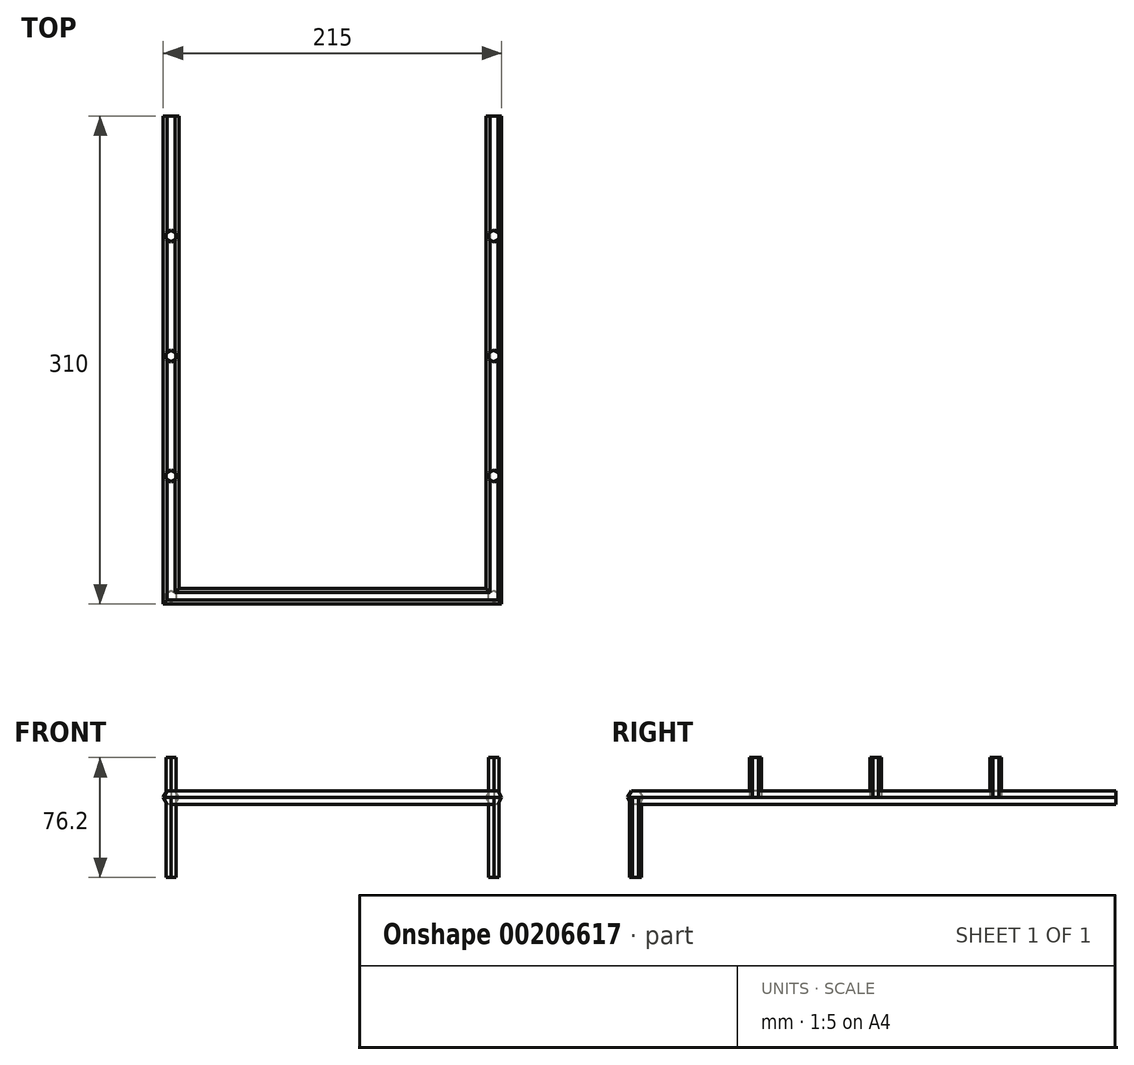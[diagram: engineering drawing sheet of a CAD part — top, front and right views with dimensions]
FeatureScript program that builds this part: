
annotation { "Feature Type Name" : "Feature", "Feature Type Description" : "" }
export const myFeature = defineFeature(function(context is Context, id is Id, definition is map)
    precondition{}
    {
        {
            var Q0;
            Q0=qCreatedBy(makeId("Top.planeOp"),FACE);
            var sketch = newSketch(context, id + "F0", { "sketchPlane" : qUnion([Q0])});
            skLineSegment(sketch, "E0.top", {"start": v(0, -305) * mm, "end": v(-205, -305) * mm});
            skLineSegment(sketch, "E0.left", {"start": v(0, 0) * mm, "end": v(0, -305) * mm});
            skLineSegment(sketch, "E0.right", {"start": v(-205, 0) * mm, "end": v(-205, -305) * mm});
            skPoint(sketch, "E1", {"position": v(0, -305) * mm});
            skPoint(sketch, "E2", {"position": v(0, 0) * mm});
            skPoint(sketch, "E3", {"position": v(0, -152.5) * mm});
            skPoint(sketch, "E4", {"position": v(-102.5, -305) * mm});
            skPoint(sketch, "E5", {"position": v(-205, -305) * mm});
            skPoint(sketch, "E6", {"position": v(-205, 0) * mm});
            skPoint(sketch, "E7", {"position": v(-205, -152.5) * mm});
            skPoint(sketch, "E8", {"position": v(0, -76.25) * mm});
            skPoint(sketch, "E9", {"position": v(-205, -76.25) * mm});
            skPoint(sketch, "E10", {"position": v(-205, -228.75) * mm});
            skPoint(sketch, "E11", {"position": v(0, -228.75) * mm});
            skPoint(sketch, "E12", {"position": v(-51.1, -305) * mm});
            skPoint(sketch, "E13", {"position": v(-153.6, -305) * mm});
            skCircle(sketch, "E14.cCircle", {"center": v(0, -76.25) * mm, "radius": 3.75 * mm, "construction": true});
            skLineSegment(sketch, "E14.0", {"start": v(0, -72.5) * mm, "end": v(3.25, -74.37) * mm});
            skLineSegment(sketch, "E14.1", {"start": v(3.25, -74.38) * mm, "end": v(3.25, -78.12) * mm});
            skLineSegment(sketch, "E14.2", {"start": v(3.25, -78.12) * mm, "end": v(0, -80) * mm});
            skLineSegment(sketch, "E14.3", {"start": v(0, -80) * mm, "end": v(-3.25, -78.13) * mm});
            skLineSegment(sketch, "E14.4", {"start": v(-3.25, -78.12) * mm, "end": v(-3.25, -74.38) * mm});
            skLineSegment(sketch, "E14.5", {"start": v(-3.25, -74.38) * mm, "end": v(0, -72.5) * mm});
            skCircle(sketch, "E15.cCircle", {"center": v(0, -228.75) * mm, "radius": 3.75 * mm, "construction": true});
            skLineSegment(sketch, "E15.0", {"start": v(0, -232.5) * mm, "end": v(-3.25, -230.62) * mm});
            skLineSegment(sketch, "E15.1", {"start": v(-3.25, -230.63) * mm, "end": v(-3.25, -226.88) * mm});
            skLineSegment(sketch, "E15.2", {"start": v(-3.25, -226.88) * mm, "end": v(0, -225) * mm});
            skLineSegment(sketch, "E15.3", {"start": v(0, -225) * mm, "end": v(3.25, -226.88) * mm});
            skLineSegment(sketch, "E15.4", {"start": v(3.25, -226.88) * mm, "end": v(3.25, -230.62) * mm});
            skLineSegment(sketch, "E15.5", {"start": v(3.25, -230.62) * mm, "end": v(0, -232.5) * mm});
            skCircle(sketch, "E16.cCircle", {"center": v(0, -152.5) * mm, "radius": 3.75 * mm, "construction": true});
            skLineSegment(sketch, "E16.0", {"start": v(0, -156.25) * mm, "end": v(-3.25, -154.38) * mm});
            skLineSegment(sketch, "E16.1", {"start": v(-3.25, -154.37) * mm, "end": v(-3.25, -150.62) * mm});
            skLineSegment(sketch, "E16.2", {"start": v(-3.25, -150.62) * mm, "end": v(0, -148.75) * mm});
            skLineSegment(sketch, "E16.3", {"start": v(0, -148.75) * mm, "end": v(3.25, -150.62) * mm});
            skLineSegment(sketch, "E16.4", {"start": v(3.25, -150.62) * mm, "end": v(3.25, -154.37) * mm});
            skLineSegment(sketch, "E16.5", {"start": v(3.25, -154.37) * mm, "end": v(0, -156.25) * mm});
            skCircle(sketch, "E17.cCircle", {"center": v(-205, -228.75) * mm, "radius": 3.75 * mm, "construction": true});
            skLineSegment(sketch, "E17.0", {"start": v(-205, -225) * mm, "end": v(-201.75, -226.88) * mm});
            skLineSegment(sketch, "E17.1", {"start": v(-201.75, -226.88) * mm, "end": v(-201.75, -230.63) * mm});
            skLineSegment(sketch, "E17.2", {"start": v(-201.75, -230.63) * mm, "end": v(-205, -232.5) * mm});
            skLineSegment(sketch, "E17.3", {"start": v(-205, -232.5) * mm, "end": v(-208.25, -230.63) * mm});
            skLineSegment(sketch, "E17.4", {"start": v(-208.25, -230.63) * mm, "end": v(-208.25, -226.88) * mm});
            skLineSegment(sketch, "E17.5", {"start": v(-208.25, -226.88) * mm, "end": v(-205, -225) * mm});
            skCircle(sketch, "E18.cCircle", {"center": v(-205, -152.5) * mm, "radius": 3.75 * mm, "construction": true});
            skLineSegment(sketch, "E18.0", {"start": v(-205, -148.75) * mm, "end": v(-201.75, -150.62) * mm});
            skLineSegment(sketch, "E18.1", {"start": v(-201.75, -150.63) * mm, "end": v(-201.75, -154.38) * mm});
            skLineSegment(sketch, "E18.2", {"start": v(-201.75, -154.38) * mm, "end": v(-205, -156.25) * mm});
            skLineSegment(sketch, "E18.3", {"start": v(-205, -156.25) * mm, "end": v(-208.25, -154.38) * mm});
            skLineSegment(sketch, "E18.4", {"start": v(-208.25, -154.38) * mm, "end": v(-208.25, -150.63) * mm});
            skLineSegment(sketch, "E18.5", {"start": v(-208.25, -150.63) * mm, "end": v(-205, -148.75) * mm});
            skCircle(sketch, "E19.cCircle", {"center": v(-205, -76.25) * mm, "radius": 3.75 * mm, "construction": true});
            skLineSegment(sketch, "E19.0", {"start": v(-205, -80) * mm, "end": v(-208.25, -78.12) * mm});
            skLineSegment(sketch, "E19.1", {"start": v(-208.25, -78.12) * mm, "end": v(-208.25, -74.38) * mm});
            skLineSegment(sketch, "E19.2", {"start": v(-208.25, -74.38) * mm, "end": v(-205, -72.5) * mm});
            skLineSegment(sketch, "E19.3", {"start": v(-205, -72.5) * mm, "end": v(-201.75, -74.38) * mm});
            skLineSegment(sketch, "E19.4", {"start": v(-201.75, -74.38) * mm, "end": v(-201.75, -78.12) * mm});
            skLineSegment(sketch, "E19.5", {"start": v(-201.75, -78.12) * mm, "end": v(-205, -80) * mm});
            skCircle(sketch, "E20.cCircle", {"center": v(-205, -305) * mm, "radius": 3.75 * mm, "construction": true});
            skLineSegment(sketch, "E20.0", {"start": v(-205, -301.25) * mm, "end": v(-201.75, -303.12) * mm});
            skLineSegment(sketch, "E20.1", {"start": v(-201.75, -303.12) * mm, "end": v(-201.75, -306.87) * mm});
            skLineSegment(sketch, "E20.2", {"start": v(-201.75, -306.87) * mm, "end": v(-205, -308.75) * mm});
            skLineSegment(sketch, "E20.3", {"start": v(-205, -308.75) * mm, "end": v(-208.25, -306.88) * mm});
            skLineSegment(sketch, "E20.4", {"start": v(-208.25, -306.88) * mm, "end": v(-208.25, -303.12) * mm});
            skLineSegment(sketch, "E20.5", {"start": v(-208.25, -303.12) * mm, "end": v(-205, -301.25) * mm});
            skCircle(sketch, "E21.cCircle", {"center": v(0, -305) * mm, "radius": 3.75 * mm, "construction": true});
            skLineSegment(sketch, "E21.0", {"start": v(0, -301.25) * mm, "end": v(3.25, -303.13) * mm});
            skLineSegment(sketch, "E21.1", {"start": v(3.25, -303.13) * mm, "end": v(3.25, -306.88) * mm});
            skLineSegment(sketch, "E21.2", {"start": v(3.25, -306.87) * mm, "end": v(0, -308.75) * mm});
            skLineSegment(sketch, "E21.3", {"start": v(0, -308.75) * mm, "end": v(-3.25, -306.87) * mm});
            skLineSegment(sketch, "E21.4", {"start": v(-3.25, -306.87) * mm, "end": v(-3.25, -303.12) * mm});
            skLineSegment(sketch, "E21.5", {"start": v(-3.25, -303.12) * mm, "end": v(0, -301.25) * mm});
            skPoint(sketch, "E22", {"position": v(0, -38.12) * mm});
            skCircle(sketch, "E23.cCircle", {"center": v(0, -38.12) * mm, "radius": 3.75 * mm, "construction": true});
            skLineSegment(sketch, "E23.0", {"start": v(0, -34.37) * mm, "end": v(3.25, -36.25) * mm});
            skLineSegment(sketch, "E23.1", {"start": v(3.25, -36.25) * mm, "end": v(3.25, -40) * mm});
            skLineSegment(sketch, "E23.2", {"start": v(3.25, -40) * mm, "end": v(0, -41.87) * mm});
            skLineSegment(sketch, "E23.3", {"start": v(0, -41.88) * mm, "end": v(-3.25, -40) * mm});
            skLineSegment(sketch, "E23.4", {"start": v(-3.25, -40) * mm, "end": v(-3.25, -36.25) * mm});
            skLineSegment(sketch, "E23.5", {"start": v(-3.25, -36.25) * mm, "end": v(0, -34.38) * mm});
            skPoint(sketch, "E24", {"position": v(-205, -36.25) * mm});
            skCircle(sketch, "E25.cCircle", {"center": v(-205, -36.25) * mm, "radius": 3.75 * mm, "construction": true});
            skLineSegment(sketch, "E25.0", {"start": v(-205, -40) * mm, "end": v(-208.25, -38.13) * mm});
            skLineSegment(sketch, "E25.1", {"start": v(-208.25, -38.13) * mm, "end": v(-208.25, -34.38) * mm});
            skLineSegment(sketch, "E25.2", {"start": v(-208.25, -34.38) * mm, "end": v(-205, -32.5) * mm});
            skLineSegment(sketch, "E25.3", {"start": v(-205, -32.5) * mm, "end": v(-201.75, -34.38) * mm});
            skLineSegment(sketch, "E25.4", {"start": v(-201.75, -34.38) * mm, "end": v(-201.75, -38.13) * mm});
            skLineSegment(sketch, "E25.5", {"start": v(-201.75, -38.13) * mm, "end": v(-205, -40) * mm});
            skSolve(sketch);
        }
        {
            var Q0;
            Q0=qCreatedBy(makeId("Front.planeOp"),FACE);
            var sketch = newSketch(context, id + "F6", { "sketchPlane" : qUnion([Q0])});
            skCircle(sketch, "E26.cCircle", {"center": v(0, 0) * mm, "radius": 5 * mm, "construction": true});
            skLineSegment(sketch, "E26.0", {"start": v(5, 0) * mm, "end": v(2.5, -4.33) * mm});
            skLineSegment(sketch, "E26.1", {"start": v(2.5, -4.33) * mm, "end": v(-2.5, -4.33) * mm});
            skLineSegment(sketch, "E26.2", {"start": v(-2.5, -4.33) * mm, "end": v(-5, 0) * mm});
            skLineSegment(sketch, "E26.3", {"start": v(-5, 0) * mm, "end": v(-2.5, 4.33) * mm});
            skLineSegment(sketch, "E26.4", {"start": v(-2.5, 4.33) * mm, "end": v(2.5, 4.33) * mm});
            skLineSegment(sketch, "E26.5", {"start": v(2.5, 4.33) * mm, "end": v(5, 0) * mm});
            skSolve(sketch);
        }
        {
            var Q0;
            Q0=makeQuery(id+"F6.imprint","IMPRINT",FACE,{"disambiguationData":[TD([[makeQuery(id+"F6.imprint","IMPRINT",EDGE,{"derivedFrom":sQuery(id+"F6.wireOp",EDGE,"E26.0")}),-1.0]])]});
            var Q1;
            Q1=sQuery(id+"F0.wireOp",EDGE,"E0.left");
            var Q2;
            Q2=sQuery(id+"F0.wireOp",EDGE,"E0.top");
            var Q3;
            Q3=sQuery(id+"F0.wireOp",EDGE,"E0.right");
            sweep(context, id + "F1", {"profiles" : qUnion([Q0]), "path" : qUnion([Q1, Q2, Q3])});
        }
        {
            var Q0;
            {var subQ2=sQuery(id+"F0.wireOp",EDGE,"E15.3");Q0=makeQuery(id+"F0.imprint","IMPRINT",FACE,{"disambiguationData":[TD([[makeQuery(id+"F0.imprint","IMPRINT",EDGE,{"derivedFrom":subQ2}),-1.0]])]});}
            var Q1;
            {var subQ0=sQuery(id+"F0.wireOp",EDGE,"E15.0");Q1=makeQuery(id+"F0.imprint","IMPRINT",FACE,{"disambiguationData":[TD([[makeQuery(id+"F0.imprint","IMPRINT",EDGE,{"derivedFrom":subQ0}),-1.0]])]});}
            var Q2;
            {var subQ2=sQuery(id+"F0.wireOp",EDGE,"E16.3");Q2=makeQuery(id+"F0.imprint","IMPRINT",FACE,{"disambiguationData":[TD([[makeQuery(id+"F0.imprint","IMPRINT",EDGE,{"derivedFrom":subQ2}),-1.0]])]});}
            var Q3;
            {var subQ0=sQuery(id+"F0.wireOp",EDGE,"E16.0");Q3=makeQuery(id+"F0.imprint","IMPRINT",FACE,{"disambiguationData":[TD([[makeQuery(id+"F0.imprint","IMPRINT",EDGE,{"derivedFrom":subQ0}),-1.0]])]});}
            var Q4;
            {var subQ0=sQuery(id+"F0.wireOp",EDGE,"E14.0");Q4=makeQuery(id+"F0.imprint","IMPRINT",FACE,{"disambiguationData":[TD([[makeQuery(id+"F0.imprint","IMPRINT",EDGE,{"derivedFrom":subQ0}),-1.0]])]});}
            var Q5;
            {var subQ2=sQuery(id+"F0.wireOp",EDGE,"E14.3");Q5=makeQuery(id+"F0.imprint","IMPRINT",FACE,{"disambiguationData":[TD([[makeQuery(id+"F0.imprint","IMPRINT",EDGE,{"derivedFrom":subQ2}),-1.0]])]});}
            var Q6;
            {var subQ0=sQuery(id+"F0.wireOp",EDGE,"E18.0");Q6=makeQuery(id+"F0.imprint","IMPRINT",FACE,{"disambiguationData":[TD([[makeQuery(id+"F0.imprint","IMPRINT",EDGE,{"derivedFrom":subQ0}),-1.0]])]});}
            var Q7;
            {var subQ2=sQuery(id+"F0.wireOp",EDGE,"E18.3");Q7=makeQuery(id+"F0.imprint","IMPRINT",FACE,{"disambiguationData":[TD([[makeQuery(id+"F0.imprint","IMPRINT",EDGE,{"derivedFrom":subQ2}),-1.0]])]});}
            var Q8;
            {var subQ0=sQuery(id+"F0.wireOp",EDGE,"E17.0");Q8=makeQuery(id+"F0.imprint","IMPRINT",FACE,{"disambiguationData":[TD([[makeQuery(id+"F0.imprint","IMPRINT",EDGE,{"derivedFrom":subQ0}),-1.0]])]});}
            var Q9;
            {var subQ2=sQuery(id+"F0.wireOp",EDGE,"E17.3");Q9=makeQuery(id+"F0.imprint","IMPRINT",FACE,{"disambiguationData":[TD([[makeQuery(id+"F0.imprint","IMPRINT",EDGE,{"derivedFrom":subQ2}),-1.0]])]});}
            var Q10;
            {var subQ2=sQuery(id+"F0.wireOp",EDGE,"E19.3");Q10=makeQuery(id+"F0.imprint","IMPRINT",FACE,{"disambiguationData":[TD([[makeQuery(id+"F0.imprint","IMPRINT",EDGE,{"derivedFrom":subQ2}),-1.0]])]});}
            var Q11;
            {var subQ0=sQuery(id+"F0.wireOp",EDGE,"E19.0");Q11=makeQuery(id+"F0.imprint","IMPRINT",FACE,{"disambiguationData":[TD([[makeQuery(id+"F0.imprint","IMPRINT",EDGE,{"derivedFrom":subQ0}),-1.0]])]});}
            extrude(context, id + "F2", {"entities" : qUnion([Q0, Q1, Q2, Q3, Q4, Q5, Q6, Q7, Q8, Q9, Q10, Q11]), "depth" : 25.4 * mm});
        }
        {
            var Q0;
            {var subQ3=sQuery(id+"F0.wireOp",EDGE,"E21.0");Q0=makeQuery(id+"F0.imprint","IMPRINT",FACE,{"disambiguationData":[TD([[makeQuery(id+"F0.imprint","IMPRINT",EDGE,{"derivedFrom":subQ3}),-1.0]])]});}
            var Q1;
            {var subQ5=sQuery(id+"F0.wireOp",EDGE,"E21.5");Q1=makeQuery(id+"F0.imprint","IMPRINT",FACE,{"disambiguationData":[TD([[makeQuery(id+"F0.imprint","IMPRINT",EDGE,{"derivedFrom":subQ5}),-1.0]])]});}
            var Q2;
            {var subQ5=sQuery(id+"F0.wireOp",EDGE,"E20.0");Q2=makeQuery(id+"F0.imprint","IMPRINT",FACE,{"disambiguationData":[TD([[makeQuery(id+"F0.imprint","IMPRINT",EDGE,{"derivedFrom":subQ5}),-1.0]])]});}
            var Q3;
            {var subQ0=sQuery(id+"F0.wireOp",EDGE,"E20.2");Q3=makeQuery(id+"F0.imprint","IMPRINT",FACE,{"disambiguationData":[TD([[makeQuery(id+"F0.imprint","IMPRINT",EDGE,{"derivedFrom":subQ0}),-1.0]])]});}
            extrude(context, id + "F3", {"entities" : qUnion([Q0, Q1, Q2, Q3]), "oppositeDirection" : true, "depth" : 50.8 * mm});
        }
        {
            var Q0;
            Q0=qCreatedBy(makeId("Right.planeOp"),FACE);
            var sketch = newSketch(context, id + "F4", { "sketchPlane" : qUnion([Q0])});
            skPoint(sketch, "E27.0", {"position": v(-76.25, 0) * mm});
            skPoint(sketch, "E28.0", {"position": v(-152.5, 0) * mm});
            skPoint(sketch, "E29.0", {"position": v(-228.75, 0) * mm});
            skSolve(sketch);
        }
    });
